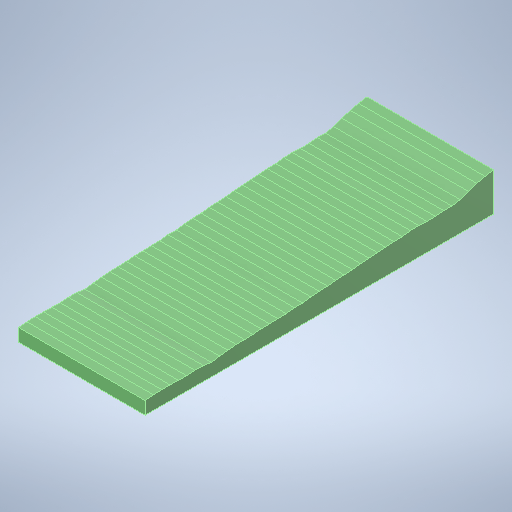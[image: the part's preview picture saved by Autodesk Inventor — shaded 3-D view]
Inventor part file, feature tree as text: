
AUTODESK INVENTOR PART (.ipt)
format: ipt  version: 2025 (Build 290162010, 162A)  size: 373,760 bytes
history: native  units: in
note: dims shown in document units (in); Inventor stores cm internally (conversion verified against a paired STEP export)
features: extrude x2, plane x2, sketch x2
ambient origin geometry x8: Origin, YZ Plane, XZ Plane, XY Plane, X Axis, Y Axis, Z Axis, Center Point
bodies: Solid1 (feature_tree)
feature tree (6):
  extrude  "Extrusion1"  Depth=456.0in
  plane  "Work Plane1"
  plane  "Work Plane2"
  extrude  "Extrusion4"  Depth=182.4in
  sketch  "Sketch1"  dims[d4=48.0in d5=456.0in]
  sketch  "Sketch4"  dims[d6=14.5in d8=1.25in d10=12.0in d14=3.5in d15=12.0in d16=12.0in d17=10.25in d18=6.25in d20=12.0in d21=16.75in d22=12.0in d23=16.375in d24=12.0in d25=17.5in d26=12.0in d27=18.0in d28=12.0in d29=17.0in d30=12.0in d31=17.5in d32=12.0in d33=19.0in d34=12.0in d35=19.25in d36=12.0in d37=20.25in d39=12.0in d40=20.875in d41=12.0in d42=21.8125in d43=12.0in d44=22.875in d45=12.0in d46=24.375in d47=12.0in d48=25.0in d49=12.0in d50=25.75in d51=12.0in d52=27.0in d53=12.0in d54=27.375in d55=12.0in d56=28.5in d57=12.0in d58=30.25in d59=12.0in d60=30.0in d61=12.0in d62=31.5in d63=12.0in d64=31.75in d65=12.0in d66=32.25in d67=12.0in d68=32.5in d69=12.0in d70=33.5in d71=12.0in d72=34.0in d73=12.0in d74=34.0in d75=12.0in d76=35.25in d77=12.0in d78=36.625in d79=12.0in d80=38.5in d81=12.0in d82=36.625in d83=12.0in d84=36.5in d85=12.0in d86=37.375in d87=12.0in d88=37.0in d89=12.0in d90=36.75in d91=12.0in d92=36.75in d93=12.0in d94=37.125in d95=12.0in d96=38.2928in d97=182.4in d98=0.0in d99=90.0deg d100=18.219in d112=125.0625in d113=0.156in d114=289.0in d115=18.0in d116=0.0in d117=0.0in]
